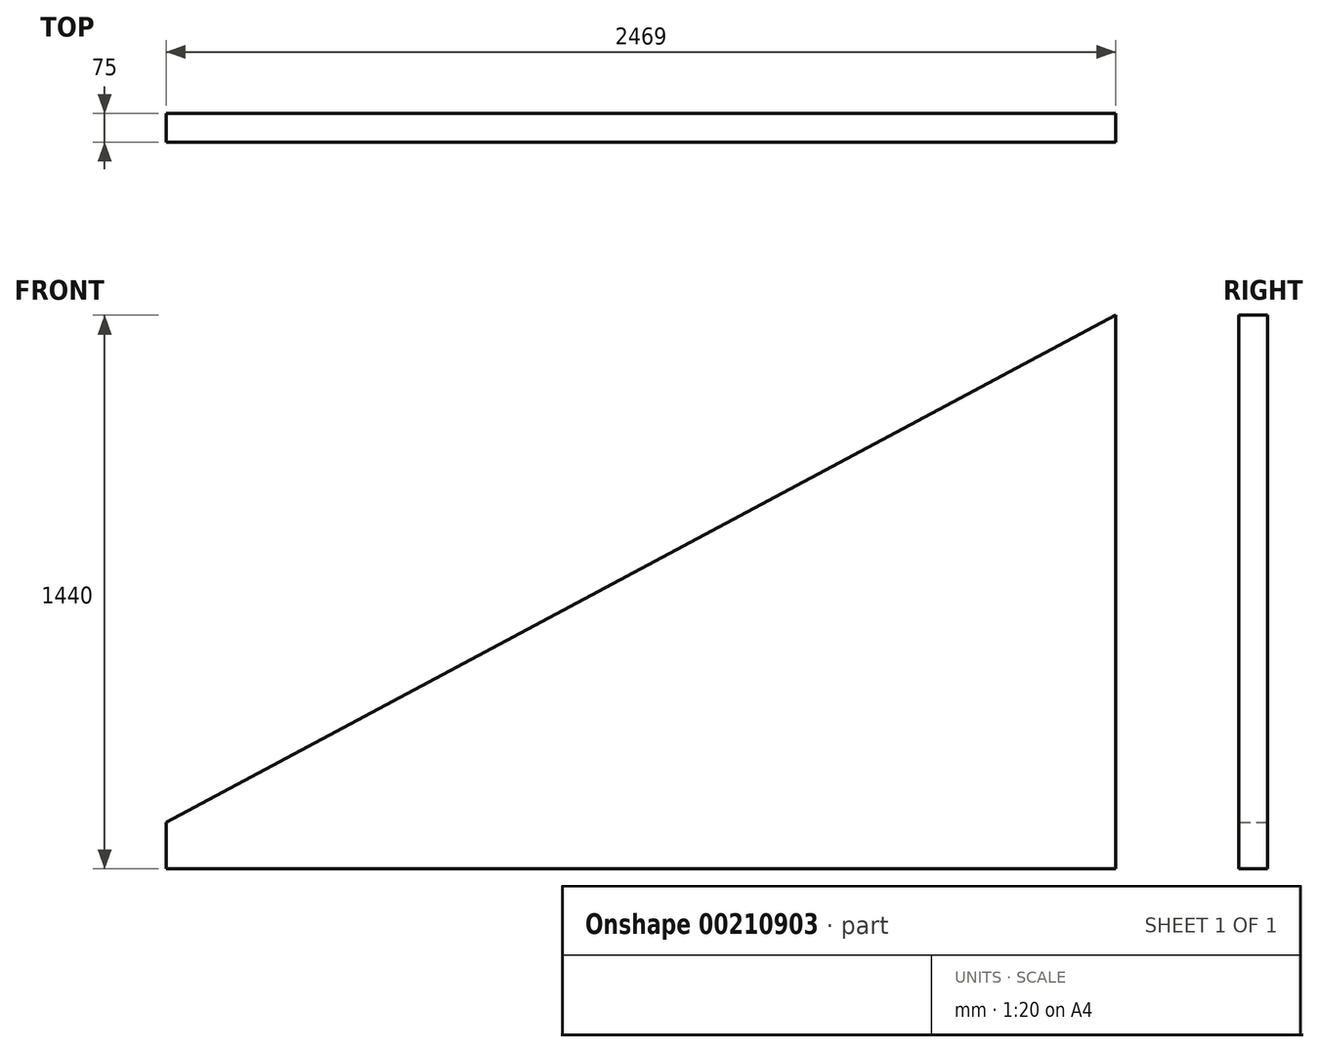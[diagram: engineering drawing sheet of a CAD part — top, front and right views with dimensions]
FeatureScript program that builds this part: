
annotation { "Feature Type Name" : "Feature", "Feature Type Description" : "" }
export const myFeature = defineFeature(function(context is Context, id is Id, definition is map)
    precondition{}
    {
        {
            var Q0;
            Q0=qCreatedBy(makeId("Front.planeOp"),FACE);
            var sketch = newSketch(context, id + "F0", { "sketchPlane" : qUnion([Q0])});
            skLineSegment(sketch, "E0.bottom", {"start": v(0, 0) * mm, "end": v(2469, 0) * mm});
            skLineSegment(sketch, "E0.right", {"start": v(2469, 0) * mm, "end": v(2469, 1440) * mm});
            skLineSegment(sketch, "E1", {"start": v(0, 0) * mm, "end": v(0, 121.02) * mm});
            skLineSegment(sketch, "E2", {"start": v(0, 121.02) * mm, "end": v(2469, 1440) * mm});
            skLineSegment(sketch, "E3", {"start": v(0, 45) * mm, "end": v(2469, 45) * mm, "construction": true});
            skLineSegment(sketch, "E4.0", {"start": v(0, 70) * mm, "end": v(2469, 1388.98) * mm, "construction": true});
            skSolve(sketch);
        }
        {
            var Q0;
            Q0=makeQuery(id+"F0.imprint","IMPRINT",FACE,{"disambiguationData":[TD([[makeQuery(id+"F0.imprint","IMPRINT",EDGE,{"derivedFrom":sQuery(id+"F0.wireOp",EDGE,"E0.bottom")}),1.0]])]});
            extrude(context, id + "F1", {"entities" : qUnion([Q0]), "depth" : 75 * mm});
        }
    });
